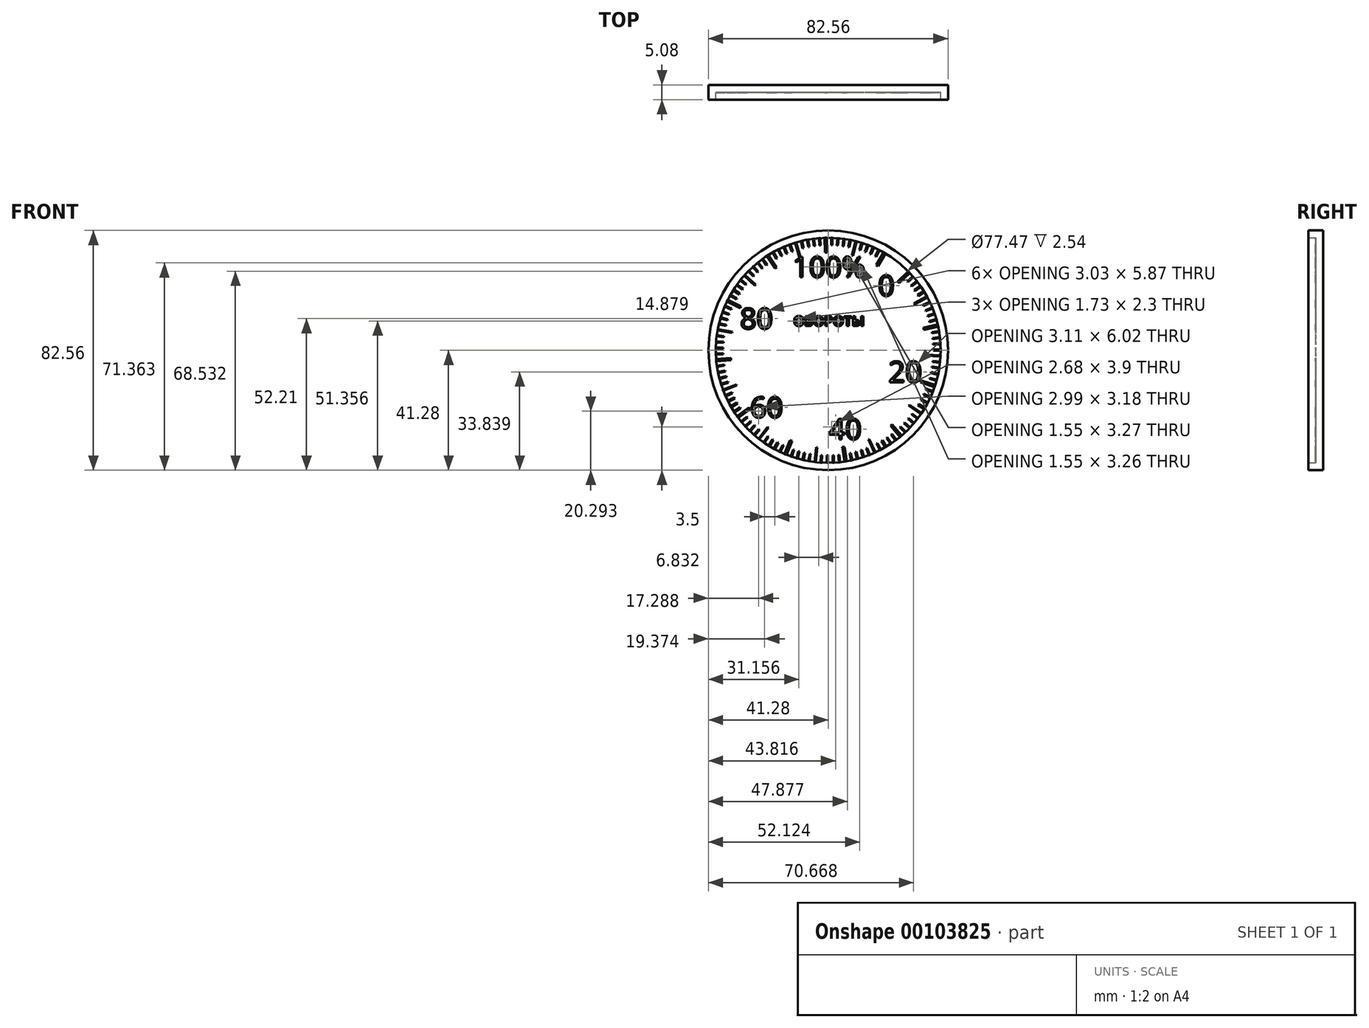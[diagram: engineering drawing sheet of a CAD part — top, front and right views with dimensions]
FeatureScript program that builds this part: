
annotation { "Feature Type Name" : "Feature", "Feature Type Description" : "" }
export const myFeature = defineFeature(function(context is Context, id is Id, definition is map)
    precondition{}
    {
        {
            var Q0;
            Q0=qCreatedBy(makeId("Front.planeOp"),FACE);
            var sketch = newSketch(context, id + "F0", { "sketchPlane" : qUnion([Q0])});
            skCircle(sketch, "E0", {"center": v(0, 0) * mm, "radius": 41.28 * mm});
            skSolve(sketch);
        }
        {
            var Q0;
            Q0=makeQuery(id+"F0.imprint","IMPRINT",FACE,{"disambiguationData":[TD([[makeQuery(id+"F0.imprint","IMPRINT",EDGE,{"derivedFrom":sQuery(id+"F0.wireOp",EDGE,"E0")}),1.0]])]});
            extrude(context, id + "F1", {"entities" : qUnion([Q0]), "depth" : 2.54 * mm});
        }
        {
            var Q0;
            Q0=makeQuery(id+"F1.opExtrude","CAP_FACE",FACE,{"disambiguationData":[OSD([sQuery(id+"F0.wireOp",EDGE,"E0")])],"isStart":false});
            var sketch = newSketch(context, id + "F2", { "sketchPlane" : qUnion([Q0])});
            skCircle(sketch, "E1.0", {"center": v(0, 0) * mm, "radius": 41.28 * mm});
            skCircle(sketch, "E2", {"center": v(0, 0) * mm, "radius": 38.74 * mm});
            skSolve(sketch);
        }
        {
            var Q0;
            Q0=makeQuery(id+"F2.imprint","IMPRINT",FACE,{"disambiguationData":[TD([[makeQuery(id+"F2.imprint","IMPRINT",EDGE,{"derivedFrom":sQuery(id+"F2.wireOp",EDGE,"E1.0")}),1.0]])]});
            extrude(context, id + "F3", {"entities" : qUnion([Q0]), "operationType" : NewBodyOperationType.ADD, "depth" : 2.54 * mm});
        }
        {
            var Q0;
            Q0=makeQuery(id+"F1.opExtrude","CAP_FACE",FACE,{"disambiguationData":[OSD([sQuery(id+"F0.wireOp",EDGE,"E0")])],"isStart":false});
            var sketch = newSketch(context, id + "F4", { "sketchPlane" : qUnion([Q0])});
            skLineSegment(sketch, "E3", {"start": v(0, 38.74) * mm, "end": v(0, -38.74) * mm, "construction": true});
            skLineSegment(sketch, "E4", {"start": v(0, 0) * mm, "end": v(27.86, 26.9) * mm, "construction": true});
            skLineSegment(sketch, "E5", {"start": v(27.6, 27.18) * mm, "end": v(23.94, 23.65) * mm, "construction": true});
            skLineSegment(sketch, "E6", {"start": v(23.94, 23.65) * mm, "end": v(24.47, 23.1) * mm, "construction": true});
            skLineSegment(sketch, "E7", {"start": v(24.47, 23.1) * mm, "end": v(28.13, 26.63) * mm, "construction": true});
            skLineSegment(sketch, "E8", {"start": v(28.13, 26.63) * mm, "end": v(27.6, 27.18) * mm, "construction": true});
            skLineSegment(sketch, "E9", {"start": v(27.73, 27.04) * mm, "end": v(24.08, 23.51) * mm, "construction": true});
            skLineSegment(sketch, "E10", {"start": v(24.08, 23.51) * mm, "end": v(24.34, 23.24) * mm, "construction": true});
            skLineSegment(sketch, "E11", {"start": v(24.34, 23.24) * mm, "end": v(28, 26.77) * mm, "construction": true});
            skLineSegment(sketch, "E12", {"start": v(28, 26.77) * mm, "end": v(27.73, 27.04) * mm});
            skPoint(sketch, "E13", {"position": v(24.2, 23.38) * mm});
            skLineSegment(sketch, "E14", {"start": v(27.73, 27.04) * mm, "end": v(25.9, 25.28) * mm});
            skLineSegment(sketch, "E15", {"start": v(25.9, 25.28) * mm, "end": v(26.17, 25) * mm});
            skLineSegment(sketch, "E16", {"start": v(26.17, 25) * mm, "end": v(28, 26.77) * mm});
            skLineSegment(sketch, "E17.1.0", {"start": v(27.5, 23.54) * mm, "end": v(29.41, 25.2) * mm});
            skLineSegment(sketch, "E17.1.1", {"start": v(29.41, 25.2) * mm, "end": v(29.17, 25.5) * mm});
            skLineSegment(sketch, "E17.1.2", {"start": v(29.17, 25.5) * mm, "end": v(27.24, 23.83) * mm});
            skLineSegment(sketch, "E17.1.3", {"start": v(27.24, 23.83) * mm, "end": v(27.5, 23.54) * mm});
            skLineSegment(sketch, "E17.2.0", {"start": v(28.74, 22) * mm, "end": v(30.75, 23.56) * mm});
            skLineSegment(sketch, "E17.2.1", {"start": v(30.75, 23.56) * mm, "end": v(30.51, 23.86) * mm});
            skLineSegment(sketch, "E17.2.2", {"start": v(30.51, 23.86) * mm, "end": v(28.5, 22.3) * mm});
            skLineSegment(sketch, "E17.2.3", {"start": v(28.5, 22.3) * mm, "end": v(28.74, 22) * mm});
            skLineSegment(sketch, "E17.3.0", {"start": v(29.9, 20.4) * mm, "end": v(31.99, 21.85) * mm});
            skLineSegment(sketch, "E17.3.1", {"start": v(31.99, 21.85) * mm, "end": v(31.77, 22.16) * mm});
            skLineSegment(sketch, "E17.3.2", {"start": v(31.77, 22.16) * mm, "end": v(29.68, 20.72) * mm});
            skLineSegment(sketch, "E17.3.3", {"start": v(29.68, 20.72) * mm, "end": v(29.9, 20.4) * mm});
            skLineSegment(sketch, "E17.4.0", {"start": v(30.96, 18.74) * mm, "end": v(33.13, 20.07) * mm});
            skLineSegment(sketch, "E17.4.1", {"start": v(33.13, 20.07) * mm, "end": v(32.93, 20.4) * mm});
            skLineSegment(sketch, "E17.4.2", {"start": v(32.93, 20.4) * mm, "end": v(30.76, 19.07) * mm});
            skLineSegment(sketch, "E17.4.3", {"start": v(30.76, 19.07) * mm, "end": v(30.96, 18.74) * mm});
            skLineSegment(sketch, "E17.5.0", {"start": v(31.94, 17.03) * mm, "end": v(34.17, 18.23) * mm});
            skLineSegment(sketch, "E17.5.1", {"start": v(34.17, 18.23) * mm, "end": v(34, 18.57) * mm});
            skLineSegment(sketch, "E17.5.2", {"start": v(34, 18.57) * mm, "end": v(31.76, 17.36) * mm});
            skLineSegment(sketch, "E17.5.3", {"start": v(31.76, 17.36) * mm, "end": v(31.94, 17.03) * mm});
            skLineSegment(sketch, "E17.6.0", {"start": v(32.82, 15.26) * mm, "end": v(35.12, 16.34) * mm});
            skLineSegment(sketch, "E17.6.1", {"start": v(35.12, 16.34) * mm, "end": v(34.96, 16.69) * mm});
            skLineSegment(sketch, "E17.6.2", {"start": v(34.96, 16.69) * mm, "end": v(32.66, 15.6) * mm});
            skLineSegment(sketch, "E17.6.3", {"start": v(32.66, 15.6) * mm, "end": v(32.82, 15.26) * mm});
            skLineSegment(sketch, "E17.7.0", {"start": v(33.6, 13.45) * mm, "end": v(35.96, 14.4) * mm});
            skLineSegment(sketch, "E17.7.1", {"start": v(35.96, 14.4) * mm, "end": v(35.81, 14.76) * mm});
            skLineSegment(sketch, "E17.7.2", {"start": v(35.81, 14.76) * mm, "end": v(33.46, 13.8) * mm});
            skLineSegment(sketch, "E17.7.3", {"start": v(33.46, 13.8) * mm, "end": v(33.6, 13.45) * mm});
            skLineSegment(sketch, "E17.8.0", {"start": v(34.29, 11.6) * mm, "end": v(36.7, 12.42) * mm});
            skLineSegment(sketch, "E17.8.1", {"start": v(36.7, 12.42) * mm, "end": v(36.57, 12.78) * mm});
            skLineSegment(sketch, "E17.8.2", {"start": v(36.57, 12.78) * mm, "end": v(34.16, 11.95) * mm});
            skLineSegment(sketch, "E17.8.3", {"start": v(34.16, 11.95) * mm, "end": v(34.29, 11.6) * mm});
            skLineSegment(sketch, "E17.9.0", {"start": v(34.87, 9.7) * mm, "end": v(37.31, 10.4) * mm});
            skLineSegment(sketch, "E17.9.1", {"start": v(37.31, 10.4) * mm, "end": v(37.2, 10.77) * mm});
            skLineSegment(sketch, "E17.9.2", {"start": v(37.2, 10.77) * mm, "end": v(34.76, 10.07) * mm});
            skLineSegment(sketch, "E17.9.3", {"start": v(34.76, 10.07) * mm, "end": v(34.87, 9.7) * mm});
            skLineSegment(sketch, "E17.10.0", {"start": v(35.35, 7.79) * mm, "end": v(37.82, 8.35) * mm});
            skLineSegment(sketch, "E17.10.1", {"start": v(37.82, 8.35) * mm, "end": v(37.74, 8.72) * mm});
            skLineSegment(sketch, "E17.10.2", {"start": v(37.74, 8.72) * mm, "end": v(35.26, 8.16) * mm});
            skLineSegment(sketch, "E17.10.3", {"start": v(35.26, 8.16) * mm, "end": v(35.35, 7.79) * mm});
            skLineSegment(sketch, "E17.11.0", {"start": v(35.72, 5.85) * mm, "end": v(38.22, 6.27) * mm});
            skLineSegment(sketch, "E17.11.1", {"start": v(38.22, 6.27) * mm, "end": v(38.16, 6.65) * mm});
            skLineSegment(sketch, "E17.11.2", {"start": v(38.16, 6.65) * mm, "end": v(35.66, 6.22) * mm});
            skLineSegment(sketch, "E17.11.3", {"start": v(35.66, 6.22) * mm, "end": v(35.72, 5.85) * mm});
            skLineSegment(sketch, "E17.12.0", {"start": v(35.98, 3.9) * mm, "end": v(38.5, 4.18) * mm});
            skLineSegment(sketch, "E17.12.1", {"start": v(38.5, 4.18) * mm, "end": v(38.47, 4.56) * mm});
            skLineSegment(sketch, "E17.12.2", {"start": v(38.47, 4.56) * mm, "end": v(35.94, 4.27) * mm});
            skLineSegment(sketch, "E17.12.3", {"start": v(35.94, 4.27) * mm, "end": v(35.98, 3.9) * mm});
            skLineSegment(sketch, "E17.13.0", {"start": v(36.14, 1.92) * mm, "end": v(38.68, 2.07) * mm});
            skLineSegment(sketch, "E17.13.1", {"start": v(38.68, 2.07) * mm, "end": v(38.66, 2.45) * mm});
            skLineSegment(sketch, "E17.13.2", {"start": v(38.66, 2.45) * mm, "end": v(36.12, 2.3) * mm});
            skLineSegment(sketch, "E17.13.3", {"start": v(36.12, 2.3) * mm, "end": v(36.14, 1.92) * mm});
            skLineSegment(sketch, "E17.14.0", {"start": v(36.2, -0.05) * mm, "end": v(38.73, -0.04) * mm});
            skLineSegment(sketch, "E17.14.1", {"start": v(38.73, -0.04) * mm, "end": v(38.73, 0.34) * mm});
            skLineSegment(sketch, "E17.14.2", {"start": v(38.73, 0.34) * mm, "end": v(36.2, 0.33) * mm});
            skLineSegment(sketch, "E17.14.3", {"start": v(36.2, 0.33) * mm, "end": v(36.2, -0.05) * mm});
            skLineSegment(sketch, "E17.15.0", {"start": v(36.14, -2.03) * mm, "end": v(38.67, -2.16) * mm});
            skLineSegment(sketch, "E17.15.1", {"start": v(38.67, -2.16) * mm, "end": v(38.7, -1.78) * mm});
            skLineSegment(sketch, "E17.15.2", {"start": v(38.7, -1.78) * mm, "end": v(36.16, -1.65) * mm});
            skLineSegment(sketch, "E17.15.3", {"start": v(36.16, -1.65) * mm, "end": v(36.14, -2.03) * mm});
            skLineSegment(sketch, "E17.16.0", {"start": v(35.97, -4) * mm, "end": v(38.5, -4.26) * mm});
            skLineSegment(sketch, "E17.16.1", {"start": v(38.5, -4.26) * mm, "end": v(38.54, -3.88) * mm});
            skLineSegment(sketch, "E17.16.2", {"start": v(38.54, -3.88) * mm, "end": v(36.01, -3.62) * mm});
            skLineSegment(sketch, "E17.16.3", {"start": v(36.01, -3.62) * mm, "end": v(35.97, -4) * mm});
            skLineSegment(sketch, "E17.17.0", {"start": v(35.7, -5.95) * mm, "end": v(38.2, -6.36) * mm});
            skLineSegment(sketch, "E17.17.1", {"start": v(38.2, -6.36) * mm, "end": v(38.27, -5.98) * mm});
            skLineSegment(sketch, "E17.17.2", {"start": v(38.27, -5.98) * mm, "end": v(35.76, -5.58) * mm});
            skLineSegment(sketch, "E17.17.3", {"start": v(35.76, -5.58) * mm, "end": v(35.7, -5.95) * mm});
            skLineSegment(sketch, "E17.18.0", {"start": v(35.32, -7.9) * mm, "end": v(37.8, -8.43) * mm});
            skLineSegment(sketch, "E17.18.1", {"start": v(37.8, -8.43) * mm, "end": v(37.89, -8.06) * mm});
            skLineSegment(sketch, "E17.18.2", {"start": v(37.89, -8.06) * mm, "end": v(35.4, -7.52) * mm});
            skLineSegment(sketch, "E17.18.3", {"start": v(35.4, -7.52) * mm, "end": v(35.32, -7.9) * mm});
            skLineSegment(sketch, "E17.19.0", {"start": v(34.84, -9.8) * mm, "end": v(37.29, -10.48) * mm});
            skLineSegment(sketch, "E17.19.1", {"start": v(37.29, -10.48) * mm, "end": v(37.4, -10.11) * mm});
            skLineSegment(sketch, "E17.19.2", {"start": v(37.4, -10.11) * mm, "end": v(34.94, -9.44) * mm});
            skLineSegment(sketch, "E17.19.3", {"start": v(34.94, -9.44) * mm, "end": v(34.84, -9.8) * mm});
            skLineSegment(sketch, "E17.20.0", {"start": v(34.25, -11.7) * mm, "end": v(36.66, -12.5) * mm});
            skLineSegment(sketch, "E17.20.1", {"start": v(36.66, -12.5) * mm, "end": v(36.78, -12.14) * mm});
            skLineSegment(sketch, "E17.20.2", {"start": v(36.78, -12.14) * mm, "end": v(34.37, -11.33) * mm});
            skLineSegment(sketch, "E17.20.3", {"start": v(34.37, -11.33) * mm, "end": v(34.25, -11.7) * mm});
            skLineSegment(sketch, "E17.21.0", {"start": v(33.56, -13.54) * mm, "end": v(35.93, -14.48) * mm});
            skLineSegment(sketch, "E17.21.1", {"start": v(35.93, -14.48) * mm, "end": v(36.07, -14.13) * mm});
            skLineSegment(sketch, "E17.21.2", {"start": v(36.07, -14.13) * mm, "end": v(33.7, -13.19) * mm});
            skLineSegment(sketch, "E17.21.3", {"start": v(33.7, -13.19) * mm, "end": v(33.56, -13.54) * mm});
            skLineSegment(sketch, "E17.22.0", {"start": v(32.78, -15.35) * mm, "end": v(35.08, -16.42) * mm});
            skLineSegment(sketch, "E17.22.1", {"start": v(35.08, -16.42) * mm, "end": v(35.24, -16.07) * mm});
            skLineSegment(sketch, "E17.22.2", {"start": v(35.24, -16.07) * mm, "end": v(32.94, -15) * mm});
            skLineSegment(sketch, "E17.22.3", {"start": v(32.94, -15) * mm, "end": v(32.78, -15.35) * mm});
            skLineSegment(sketch, "E17.23.0", {"start": v(31.89, -17.12) * mm, "end": v(34.13, -18.3) * mm});
            skLineSegment(sketch, "E17.23.1", {"start": v(34.13, -18.3) * mm, "end": v(34.31, -17.97) * mm});
            skLineSegment(sketch, "E17.23.2", {"start": v(34.31, -17.97) * mm, "end": v(32.07, -16.78) * mm});
            skLineSegment(sketch, "E17.23.3", {"start": v(32.07, -16.78) * mm, "end": v(31.89, -17.12) * mm});
            skLineSegment(sketch, "E17.24.0", {"start": v(30.9, -18.83) * mm, "end": v(33.08, -20.14) * mm});
            skLineSegment(sketch, "E17.24.1", {"start": v(33.08, -20.14) * mm, "end": v(33.28, -19.82) * mm});
            skLineSegment(sketch, "E17.24.2", {"start": v(33.28, -19.82) * mm, "end": v(31.1, -18.5) * mm});
            skLineSegment(sketch, "E17.24.3", {"start": v(31.1, -18.5) * mm, "end": v(30.9, -18.83) * mm});
            skLineSegment(sketch, "E17.25.0", {"start": v(29.83, -20.5) * mm, "end": v(31.94, -21.92) * mm});
            skLineSegment(sketch, "E17.25.1", {"start": v(31.94, -21.92) * mm, "end": v(32.15, -21.6) * mm});
            skLineSegment(sketch, "E17.25.2", {"start": v(32.15, -21.6) * mm, "end": v(30.05, -20.18) * mm});
            skLineSegment(sketch, "E17.25.3", {"start": v(30.05, -20.18) * mm, "end": v(29.83, -20.5) * mm});
            skLineSegment(sketch, "E17.26.0", {"start": v(28.67, -22.09) * mm, "end": v(30.7, -23.63) * mm});
            skLineSegment(sketch, "E17.26.1", {"start": v(30.7, -23.63) * mm, "end": v(30.92, -23.33) * mm});
            skLineSegment(sketch, "E17.26.2", {"start": v(30.92, -23.33) * mm, "end": v(28.9, -21.79) * mm});
            skLineSegment(sketch, "E17.26.3", {"start": v(28.9, -21.79) * mm, "end": v(28.67, -22.09) * mm});
            skLineSegment(sketch, "E17.27.0", {"start": v(27.42, -23.62) * mm, "end": v(29.36, -25.27) * mm});
            skLineSegment(sketch, "E17.27.1", {"start": v(29.36, -25.27) * mm, "end": v(29.6, -24.98) * mm});
            skLineSegment(sketch, "E17.27.2", {"start": v(29.6, -24.98) * mm, "end": v(27.67, -23.33) * mm});
            skLineSegment(sketch, "E17.27.3", {"start": v(27.67, -23.33) * mm, "end": v(27.42, -23.62) * mm});
            skLineSegment(sketch, "E17.28.0", {"start": v(26.1, -25.08) * mm, "end": v(27.94, -26.83) * mm});
            skLineSegment(sketch, "E17.28.1", {"start": v(27.94, -26.83) * mm, "end": v(28.2, -26.56) * mm});
            skLineSegment(sketch, "E17.28.2", {"start": v(28.2, -26.56) * mm, "end": v(26.36, -24.8) * mm});
            skLineSegment(sketch, "E17.28.3", {"start": v(26.36, -24.8) * mm, "end": v(26.1, -25.08) * mm});
            skLineSegment(sketch, "E17.29.0", {"start": v(24.69, -26.47) * mm, "end": v(26.43, -28.32) * mm});
            skLineSegment(sketch, "E17.29.1", {"start": v(26.43, -28.32) * mm, "end": v(26.7, -28.06) * mm});
            skLineSegment(sketch, "E17.29.2", {"start": v(26.7, -28.06) * mm, "end": v(24.97, -26.2) * mm});
            skLineSegment(sketch, "E17.29.3", {"start": v(24.97, -26.2) * mm, "end": v(24.69, -26.47) * mm});
            skLineSegment(sketch, "E17.30.0", {"start": v(23.2, -27.78) * mm, "end": v(24.85, -29.72) * mm});
            skLineSegment(sketch, "E17.30.1", {"start": v(24.85, -29.72) * mm, "end": v(25.14, -29.47) * mm});
            skLineSegment(sketch, "E17.30.2", {"start": v(25.14, -29.47) * mm, "end": v(23.5, -27.53) * mm});
            skLineSegment(sketch, "E17.30.3", {"start": v(23.5, -27.53) * mm, "end": v(23.2, -27.78) * mm});
            skLineSegment(sketch, "E17.31.0", {"start": v(21.66, -29) * mm, "end": v(23.19, -31.03) * mm});
            skLineSegment(sketch, "E17.31.1", {"start": v(23.19, -31.03) * mm, "end": v(23.5, -30.8) * mm});
            skLineSegment(sketch, "E17.31.2", {"start": v(23.5, -30.8) * mm, "end": v(21.96, -28.77) * mm});
            skLineSegment(sketch, "E17.31.3", {"start": v(21.96, -28.77) * mm, "end": v(21.66, -29) * mm});
            skLineSegment(sketch, "E17.32.0", {"start": v(20.04, -30.14) * mm, "end": v(21.46, -32.25) * mm});
            skLineSegment(sketch, "E17.32.1", {"start": v(21.46, -32.25) * mm, "end": v(21.78, -32.03) * mm});
            skLineSegment(sketch, "E17.32.2", {"start": v(21.78, -32.03) * mm, "end": v(20.36, -29.93) * mm});
            skLineSegment(sketch, "E17.32.3", {"start": v(20.36, -29.93) * mm, "end": v(20.04, -30.14) * mm});
            skLineSegment(sketch, "E17.33.0", {"start": v(18.37, -31.19) * mm, "end": v(19.67, -33.37) * mm});
            skLineSegment(sketch, "E17.33.1", {"start": v(19.67, -33.37) * mm, "end": v(20, -33.17) * mm});
            skLineSegment(sketch, "E17.33.2", {"start": v(20, -33.17) * mm, "end": v(18.7, -31) * mm});
            skLineSegment(sketch, "E17.33.3", {"start": v(18.7, -31) * mm, "end": v(18.37, -31.19) * mm});
            skLineSegment(sketch, "E17.34.0", {"start": v(16.64, -32.14) * mm, "end": v(17.82, -34.4) * mm});
            skLineSegment(sketch, "E17.34.1", {"start": v(17.82, -34.4) * mm, "end": v(18.16, -34.22) * mm});
            skLineSegment(sketch, "E17.34.2", {"start": v(18.16, -34.22) * mm, "end": v(16.98, -31.97) * mm});
            skLineSegment(sketch, "E17.34.3", {"start": v(16.98, -31.97) * mm, "end": v(16.64, -32.14) * mm});
            skLineSegment(sketch, "E17.35.0", {"start": v(14.86, -33) * mm, "end": v(15.92, -35.31) * mm});
            skLineSegment(sketch, "E17.35.1", {"start": v(15.92, -35.31) * mm, "end": v(16.26, -35.16) * mm});
            skLineSegment(sketch, "E17.35.2", {"start": v(16.26, -35.16) * mm, "end": v(15.2, -32.84) * mm});
            skLineSegment(sketch, "E17.35.3", {"start": v(15.2, -32.84) * mm, "end": v(14.86, -33) * mm});
            skLineSegment(sketch, "E17.36.0", {"start": v(13.04, -33.76) * mm, "end": v(13.97, -36.13) * mm});
            skLineSegment(sketch, "E17.36.1", {"start": v(13.97, -36.13) * mm, "end": v(14.32, -35.99) * mm});
            skLineSegment(sketch, "E17.36.2", {"start": v(14.32, -35.99) * mm, "end": v(13.4, -33.62) * mm});
            skLineSegment(sketch, "E17.36.3", {"start": v(13.4, -33.62) * mm, "end": v(13.04, -33.76) * mm});
            skLineSegment(sketch, "E17.37.0", {"start": v(11.18, -34.42) * mm, "end": v(11.98, -36.84) * mm});
            skLineSegment(sketch, "E17.37.1", {"start": v(11.98, -36.84) * mm, "end": v(12.34, -36.72) * mm});
            skLineSegment(sketch, "E17.37.2", {"start": v(12.34, -36.72) * mm, "end": v(11.54, -34.3) * mm});
            skLineSegment(sketch, "E17.37.3", {"start": v(11.54, -34.3) * mm, "end": v(11.18, -34.42) * mm});
            skLineSegment(sketch, "E17.38.0", {"start": v(9.28, -34.98) * mm, "end": v(9.95, -37.44) * mm});
            skLineSegment(sketch, "E17.38.1", {"start": v(9.95, -37.44) * mm, "end": v(10.32, -37.34) * mm});
            skLineSegment(sketch, "E17.38.2", {"start": v(10.32, -37.34) * mm, "end": v(9.65, -34.88) * mm});
            skLineSegment(sketch, "E17.38.3", {"start": v(9.65, -34.88) * mm, "end": v(9.28, -34.98) * mm});
            skLineSegment(sketch, "E17.39.0", {"start": v(7.36, -35.44) * mm, "end": v(7.9, -37.92) * mm});
            skLineSegment(sketch, "E17.39.1", {"start": v(7.9, -37.92) * mm, "end": v(8.26, -37.84) * mm});
            skLineSegment(sketch, "E17.39.2", {"start": v(8.26, -37.84) * mm, "end": v(7.73, -35.36) * mm});
            skLineSegment(sketch, "E17.39.3", {"start": v(7.73, -35.36) * mm, "end": v(7.36, -35.44) * mm});
            skLineSegment(sketch, "E17.40.0", {"start": v(5.42, -35.79) * mm, "end": v(5.81, -38.3) * mm});
            skLineSegment(sketch, "E17.40.1", {"start": v(5.81, -38.3) * mm, "end": v(6.19, -38.24) * mm});
            skLineSegment(sketch, "E17.40.2", {"start": v(6.19, -38.24) * mm, "end": v(5.8, -35.73) * mm});
            skLineSegment(sketch, "E17.40.3", {"start": v(5.8, -35.73) * mm, "end": v(5.42, -35.79) * mm});
            skLineSegment(sketch, "E17.41.0", {"start": v(3.46, -36.03) * mm, "end": v(3.71, -38.56) * mm});
            skLineSegment(sketch, "E17.41.1", {"start": v(3.71, -38.56) * mm, "end": v(4.1, -38.52) * mm});
            skLineSegment(sketch, "E17.41.2", {"start": v(4.1, -38.52) * mm, "end": v(3.84, -36) * mm});
            skLineSegment(sketch, "E17.41.3", {"start": v(3.84, -36) * mm, "end": v(3.46, -36.03) * mm});
            skLineSegment(sketch, "E17.42.0", {"start": v(1.49, -36.16) * mm, "end": v(1.6, -38.7) * mm});
            skLineSegment(sketch, "E17.42.1", {"start": v(1.6, -38.7) * mm, "end": v(1.98, -38.68) * mm});
            skLineSegment(sketch, "E17.42.2", {"start": v(1.98, -38.68) * mm, "end": v(1.87, -36.15) * mm});
            skLineSegment(sketch, "E17.42.3", {"start": v(1.87, -36.15) * mm, "end": v(1.49, -36.16) * mm});
            skLineSegment(sketch, "E17.43.0", {"start": v(-0.49, -36.2) * mm, "end": v(-0.51, -38.73) * mm});
            skLineSegment(sketch, "E17.43.1", {"start": v(-0.51, -38.73) * mm, "end": v(-0.13, -38.73) * mm});
            skLineSegment(sketch, "E17.43.2", {"start": v(-0.13, -38.73) * mm, "end": v(-0.1, -36.2) * mm});
            skLineSegment(sketch, "E17.43.3", {"start": v(-0.1, -36.2) * mm, "end": v(-0.49, -36.2) * mm});
            skLineSegment(sketch, "E17.44.0", {"start": v(-2.46, -36.11) * mm, "end": v(-2.62, -38.65) * mm});
            skLineSegment(sketch, "E17.44.1", {"start": v(-2.62, -38.65) * mm, "end": v(-2.24, -38.67) * mm});
            skLineSegment(sketch, "E17.44.2", {"start": v(-2.24, -38.67) * mm, "end": v(-2.08, -36.13) * mm});
            skLineSegment(sketch, "E17.44.3", {"start": v(-2.08, -36.13) * mm, "end": v(-2.46, -36.11) * mm});
            skLineSegment(sketch, "E17.45.0", {"start": v(-4.43, -35.92) * mm, "end": v(-4.73, -38.45) * mm});
            skLineSegment(sketch, "E17.45.1", {"start": v(-4.73, -38.45) * mm, "end": v(-4.35, -38.5) * mm});
            skLineSegment(sketch, "E17.45.2", {"start": v(-4.35, -38.5) * mm, "end": v(-4.05, -35.97) * mm});
            skLineSegment(sketch, "E17.45.3", {"start": v(-4.05, -35.97) * mm, "end": v(-4.43, -35.92) * mm});
            skLineSegment(sketch, "E17.46.0", {"start": v(-6.38, -35.63) * mm, "end": v(-6.82, -38.13) * mm});
            skLineSegment(sketch, "E17.46.1", {"start": v(-6.82, -38.13) * mm, "end": v(-6.44, -38.2) * mm});
            skLineSegment(sketch, "E17.46.2", {"start": v(-6.44, -38.2) * mm, "end": v(-6, -35.7) * mm});
            skLineSegment(sketch, "E17.46.3", {"start": v(-6, -35.7) * mm, "end": v(-6.38, -35.63) * mm});
            skLineSegment(sketch, "E17.47.0", {"start": v(-8.32, -35.23) * mm, "end": v(-8.89, -37.7) * mm});
            skLineSegment(sketch, "E17.47.1", {"start": v(-8.89, -37.7) * mm, "end": v(-8.52, -37.79) * mm});
            skLineSegment(sketch, "E17.47.2", {"start": v(-8.52, -37.79) * mm, "end": v(-7.95, -35.31) * mm});
            skLineSegment(sketch, "E17.47.3", {"start": v(-7.95, -35.31) * mm, "end": v(-8.32, -35.23) * mm});
            skLineSegment(sketch, "E17.48.0", {"start": v(-10.23, -34.72) * mm, "end": v(-10.93, -37.16) * mm});
            skLineSegment(sketch, "E17.48.1", {"start": v(-10.93, -37.16) * mm, "end": v(-10.56, -37.27) * mm});
            skLineSegment(sketch, "E17.48.2", {"start": v(-10.56, -37.27) * mm, "end": v(-9.86, -34.83) * mm});
            skLineSegment(sketch, "E17.48.3", {"start": v(-9.86, -34.83) * mm, "end": v(-10.23, -34.72) * mm});
            skLineSegment(sketch, "E17.49.0", {"start": v(-12.1, -34.11) * mm, "end": v(-12.94, -36.5) * mm});
            skLineSegment(sketch, "E17.49.1", {"start": v(-12.94, -36.5) * mm, "end": v(-12.58, -36.63) * mm});
            skLineSegment(sketch, "E17.49.2", {"start": v(-12.58, -36.63) * mm, "end": v(-11.74, -34.24) * mm});
            skLineSegment(sketch, "E17.49.3", {"start": v(-11.74, -34.24) * mm, "end": v(-12.1, -34.11) * mm});
            skLineSegment(sketch, "E17.50.0", {"start": v(-13.95, -33.4) * mm, "end": v(-14.91, -35.75) * mm});
            skLineSegment(sketch, "E17.50.1", {"start": v(-14.91, -35.75) * mm, "end": v(-14.56, -35.9) * mm});
            skLineSegment(sketch, "E17.50.2", {"start": v(-14.56, -35.9) * mm, "end": v(-13.6, -33.54) * mm});
            skLineSegment(sketch, "E17.50.3", {"start": v(-13.6, -33.54) * mm, "end": v(-13.95, -33.4) * mm});
            skLineSegment(sketch, "E17.51.0", {"start": v(-15.75, -32.59) * mm, "end": v(-16.84, -34.88) * mm});
            skLineSegment(sketch, "E17.51.1", {"start": v(-16.84, -34.88) * mm, "end": v(-16.5, -35.05) * mm});
            skLineSegment(sketch, "E17.51.2", {"start": v(-16.5, -35.05) * mm, "end": v(-15.4, -32.75) * mm});
            skLineSegment(sketch, "E17.51.3", {"start": v(-15.4, -32.75) * mm, "end": v(-15.75, -32.59) * mm});
            skLineSegment(sketch, "E17.52.0", {"start": v(-17.5, -31.68) * mm, "end": v(-18.72, -33.91) * mm});
            skLineSegment(sketch, "E17.52.1", {"start": v(-18.72, -33.91) * mm, "end": v(-18.39, -34.1) * mm});
            skLineSegment(sketch, "E17.52.2", {"start": v(-18.39, -34.1) * mm, "end": v(-17.17, -31.86) * mm});
            skLineSegment(sketch, "E17.52.3", {"start": v(-17.17, -31.86) * mm, "end": v(-17.5, -31.68) * mm});
            skLineSegment(sketch, "E17.53.0", {"start": v(-19.2, -30.68) * mm, "end": v(-20.54, -32.84) * mm});
            skLineSegment(sketch, "E17.53.1", {"start": v(-20.54, -32.84) * mm, "end": v(-20.22, -33.04) * mm});
            skLineSegment(sketch, "E17.53.2", {"start": v(-20.22, -33.04) * mm, "end": v(-18.88, -30.88) * mm});
            skLineSegment(sketch, "E17.53.3", {"start": v(-18.88, -30.88) * mm, "end": v(-19.2, -30.68) * mm});
            skLineSegment(sketch, "E17.54.0", {"start": v(-20.85, -29.59) * mm, "end": v(-22.3, -31.67) * mm});
            skLineSegment(sketch, "E17.54.1", {"start": v(-22.3, -31.67) * mm, "end": v(-22, -31.89) * mm});
            skLineSegment(sketch, "E17.54.2", {"start": v(-22, -31.89) * mm, "end": v(-20.54, -29.8) * mm});
            skLineSegment(sketch, "E17.54.3", {"start": v(-20.54, -29.8) * mm, "end": v(-20.85, -29.59) * mm});
            skLineSegment(sketch, "E17.55.0", {"start": v(-22.43, -28.4) * mm, "end": v(-24, -30.4) * mm});
            skLineSegment(sketch, "E17.55.1", {"start": v(-24, -30.4) * mm, "end": v(-23.7, -30.64) * mm});
            skLineSegment(sketch, "E17.55.2", {"start": v(-23.7, -30.64) * mm, "end": v(-22.13, -28.64) * mm});
            skLineSegment(sketch, "E17.55.3", {"start": v(-22.13, -28.64) * mm, "end": v(-22.43, -28.4) * mm});
            skLineSegment(sketch, "E17.56.0", {"start": v(-23.95, -27.14) * mm, "end": v(-25.62, -29.05) * mm});
            skLineSegment(sketch, "E17.56.1", {"start": v(-25.62, -29.05) * mm, "end": v(-25.33, -29.3) * mm});
            skLineSegment(sketch, "E17.56.2", {"start": v(-25.33, -29.3) * mm, "end": v(-23.66, -27.39) * mm});
            skLineSegment(sketch, "E17.56.3", {"start": v(-23.66, -27.39) * mm, "end": v(-23.95, -27.14) * mm});
            skLineSegment(sketch, "E17.57.0", {"start": v(-25.4, -25.8) * mm, "end": v(-27.17, -27.61) * mm});
            skLineSegment(sketch, "E17.57.1", {"start": v(-27.17, -27.61) * mm, "end": v(-26.9, -27.88) * mm});
            skLineSegment(sketch, "E17.57.2", {"start": v(-26.9, -27.88) * mm, "end": v(-25.12, -26.06) * mm});
            skLineSegment(sketch, "E17.57.3", {"start": v(-25.12, -26.06) * mm, "end": v(-25.4, -25.8) * mm});
            skLineSegment(sketch, "E17.58.0", {"start": v(-26.76, -24.37) * mm, "end": v(-28.63, -26.09) * mm});
            skLineSegment(sketch, "E17.58.1", {"start": v(-28.63, -26.09) * mm, "end": v(-28.38, -26.37) * mm});
            skLineSegment(sketch, "E17.58.2", {"start": v(-28.38, -26.37) * mm, "end": v(-26.5, -24.65) * mm});
            skLineSegment(sketch, "E17.58.3", {"start": v(-26.5, -24.65) * mm, "end": v(-26.76, -24.37) * mm});
            skLineSegment(sketch, "E17.59.0", {"start": v(-28.05, -22.87) * mm, "end": v(-30.01, -24.49) * mm});
            skLineSegment(sketch, "E17.59.1", {"start": v(-30.01, -24.49) * mm, "end": v(-29.77, -24.78) * mm});
            skLineSegment(sketch, "E17.59.2", {"start": v(-29.77, -24.78) * mm, "end": v(-27.81, -23.16) * mm});
            skLineSegment(sketch, "E17.59.3", {"start": v(-27.81, -23.16) * mm, "end": v(-28.05, -22.87) * mm});
            skLineSegment(sketch, "E17.60.0", {"start": v(-29.26, -21.3) * mm, "end": v(-31.3, -22.81) * mm});
            skLineSegment(sketch, "E17.60.1", {"start": v(-31.3, -22.81) * mm, "end": v(-31.08, -23.12) * mm});
            skLineSegment(sketch, "E17.60.2", {"start": v(-31.08, -23.12) * mm, "end": v(-29.03, -21.61) * mm});
            skLineSegment(sketch, "E17.60.3", {"start": v(-29.03, -21.61) * mm, "end": v(-29.26, -21.3) * mm});
            skLineSegment(sketch, "E17.61.0", {"start": v(-30.38, -19.68) * mm, "end": v(-32.5, -21.07) * mm});
            skLineSegment(sketch, "E17.61.1", {"start": v(-32.5, -21.07) * mm, "end": v(-32.3, -21.39) * mm});
            skLineSegment(sketch, "E17.61.2", {"start": v(-32.3, -21.39) * mm, "end": v(-30.17, -20) * mm});
            skLineSegment(sketch, "E17.61.3", {"start": v(-30.17, -20) * mm, "end": v(-30.38, -19.68) * mm});
            skLineSegment(sketch, "E17.62.0", {"start": v(-31.4, -18) * mm, "end": v(-33.6, -19.27) * mm});
            skLineSegment(sketch, "E17.62.1", {"start": v(-33.6, -19.27) * mm, "end": v(-33.41, -19.6) * mm});
            skLineSegment(sketch, "E17.62.2", {"start": v(-33.41, -19.6) * mm, "end": v(-31.21, -18.32) * mm});
            skLineSegment(sketch, "E17.62.3", {"start": v(-31.21, -18.32) * mm, "end": v(-31.4, -18) * mm});
            skLineSegment(sketch, "E17.63.0", {"start": v(-32.34, -16.25) * mm, "end": v(-34.6, -17.4) * mm});
            skLineSegment(sketch, "E17.63.1", {"start": v(-34.6, -17.4) * mm, "end": v(-34.43, -17.74) * mm});
            skLineSegment(sketch, "E17.63.2", {"start": v(-34.43, -17.74) * mm, "end": v(-32.17, -16.6) * mm});
            skLineSegment(sketch, "E17.63.3", {"start": v(-32.17, -16.6) * mm, "end": v(-32.34, -16.25) * mm});
            skLineSegment(sketch, "E17.64.0", {"start": v(-33.18, -14.46) * mm, "end": v(-35.5, -15.5) * mm});
            skLineSegment(sketch, "E17.64.1", {"start": v(-35.5, -15.5) * mm, "end": v(-35.35, -15.84) * mm});
            skLineSegment(sketch, "E17.64.2", {"start": v(-35.35, -15.84) * mm, "end": v(-33.02, -14.81) * mm});
            skLineSegment(sketch, "E17.64.3", {"start": v(-33.02, -14.81) * mm, "end": v(-33.18, -14.46) * mm});
            skLineSegment(sketch, "E17.65.0", {"start": v(-33.92, -12.63) * mm, "end": v(-36.3, -13.53) * mm});
            skLineSegment(sketch, "E17.65.1", {"start": v(-36.3, -13.53) * mm, "end": v(-36.16, -13.89) * mm});
            skLineSegment(sketch, "E17.65.2", {"start": v(-36.16, -13.89) * mm, "end": v(-33.78, -12.99) * mm});
            skLineSegment(sketch, "E17.65.3", {"start": v(-33.78, -12.99) * mm, "end": v(-33.92, -12.63) * mm});
            skLineSegment(sketch, "E17.66.0", {"start": v(-34.56, -10.76) * mm, "end": v(-36.98, -11.53) * mm});
            skLineSegment(sketch, "E17.66.1", {"start": v(-36.98, -11.53) * mm, "end": v(-36.86, -11.9) * mm});
            skLineSegment(sketch, "E17.66.2", {"start": v(-36.86, -11.9) * mm, "end": v(-34.44, -11.13) * mm});
            skLineSegment(sketch, "E17.66.3", {"start": v(-34.44, -11.13) * mm, "end": v(-34.56, -10.76) * mm});
            skLineSegment(sketch, "E17.67.0", {"start": v(-35.1, -8.86) * mm, "end": v(-37.55, -9.5) * mm});
            skLineSegment(sketch, "E17.67.1", {"start": v(-37.55, -9.5) * mm, "end": v(-37.46, -9.86) * mm});
            skLineSegment(sketch, "E17.67.2", {"start": v(-37.46, -9.86) * mm, "end": v(-35, -9.23) * mm});
            skLineSegment(sketch, "E17.67.3", {"start": v(-35, -9.23) * mm, "end": v(-35.1, -8.86) * mm});
            skLineSegment(sketch, "E17.68.0", {"start": v(-35.52, -6.93) * mm, "end": v(-38.02, -7.43) * mm});
            skLineSegment(sketch, "E17.68.1", {"start": v(-38.02, -7.43) * mm, "end": v(-37.94, -7.8) * mm});
            skLineSegment(sketch, "E17.68.2", {"start": v(-37.94, -7.8) * mm, "end": v(-35.45, -7.3) * mm});
            skLineSegment(sketch, "E17.68.3", {"start": v(-35.45, -7.3) * mm, "end": v(-35.52, -6.93) * mm});
            skLineSegment(sketch, "E17.69.0", {"start": v(-35.85, -4.99) * mm, "end": v(-38.36, -5.35) * mm});
            skLineSegment(sketch, "E17.69.1", {"start": v(-38.36, -5.35) * mm, "end": v(-38.3, -5.73) * mm});
            skLineSegment(sketch, "E17.69.2", {"start": v(-38.3, -5.73) * mm, "end": v(-35.8, -5.36) * mm});
            skLineSegment(sketch, "E17.69.3", {"start": v(-35.8, -5.36) * mm, "end": v(-35.85, -4.99) * mm});
            skLineSegment(sketch, "E17.70.0", {"start": v(-36.07, -3.02) * mm, "end": v(-38.6, -3.25) * mm});
            skLineSegment(sketch, "E17.70.1", {"start": v(-38.6, -3.25) * mm, "end": v(-38.56, -3.63) * mm});
            skLineSegment(sketch, "E17.70.2", {"start": v(-38.56, -3.63) * mm, "end": v(-36.03, -3.4) * mm});
            skLineSegment(sketch, "E17.70.3", {"start": v(-36.03, -3.4) * mm, "end": v(-36.07, -3.02) * mm});
            skLineSegment(sketch, "E17.71.0", {"start": v(-36.18, -1.05) * mm, "end": v(-38.72, -1.14) * mm});
            skLineSegment(sketch, "E17.71.1", {"start": v(-38.72, -1.14) * mm, "end": v(-38.7, -1.52) * mm});
            skLineSegment(sketch, "E17.71.2", {"start": v(-38.7, -1.52) * mm, "end": v(-36.17, -1.43) * mm});
            skLineSegment(sketch, "E17.71.3", {"start": v(-36.17, -1.43) * mm, "end": v(-36.18, -1.05) * mm});
            skLineSegment(sketch, "E17.72.0", {"start": v(-36.18, 0.93) * mm, "end": v(-38.72, 0.98) * mm});
            skLineSegment(sketch, "E17.72.1", {"start": v(-38.72, 0.98) * mm, "end": v(-38.73, 0.6) * mm});
            skLineSegment(sketch, "E17.72.2", {"start": v(-38.73, 0.6) * mm, "end": v(-36.2, 0.54) * mm});
            skLineSegment(sketch, "E17.72.3", {"start": v(-36.2, 0.54) * mm, "end": v(-36.18, 0.93) * mm});
            skLineSegment(sketch, "E17.73.0", {"start": v(-36.08, 2.9) * mm, "end": v(-38.61, 3.09) * mm});
            skLineSegment(sketch, "E17.73.1", {"start": v(-38.61, 3.09) * mm, "end": v(-38.64, 2.7) * mm});
            skLineSegment(sketch, "E17.73.2", {"start": v(-38.64, 2.7) * mm, "end": v(-36.1, 2.52) * mm});
            skLineSegment(sketch, "E17.73.3", {"start": v(-36.1, 2.52) * mm, "end": v(-36.08, 2.9) * mm});
            skLineSegment(sketch, "E17.74.0", {"start": v(-35.87, 4.86) * mm, "end": v(-38.39, 5.19) * mm});
            skLineSegment(sketch, "E17.74.1", {"start": v(-38.39, 5.19) * mm, "end": v(-38.43, 4.81) * mm});
            skLineSegment(sketch, "E17.74.2", {"start": v(-38.43, 4.81) * mm, "end": v(-35.92, 4.48) * mm});
            skLineSegment(sketch, "E17.74.3", {"start": v(-35.92, 4.48) * mm, "end": v(-35.87, 4.86) * mm});
            skLineSegment(sketch, "E17.75.0", {"start": v(-35.55, 6.81) * mm, "end": v(-38.05, 7.28) * mm});
            skLineSegment(sketch, "E17.75.1", {"start": v(-38.05, 7.28) * mm, "end": v(-38.12, 6.9) * mm});
            skLineSegment(sketch, "E17.75.2", {"start": v(-38.12, 6.9) * mm, "end": v(-35.62, 6.44) * mm});
            skLineSegment(sketch, "E17.75.3", {"start": v(-35.62, 6.44) * mm, "end": v(-35.55, 6.81) * mm});
            skLineSegment(sketch, "E17.76.0", {"start": v(-35.12, 8.74) * mm, "end": v(-37.6, 9.34) * mm});
            skLineSegment(sketch, "E17.76.1", {"start": v(-37.6, 9.34) * mm, "end": v(-37.68, 8.97) * mm});
            skLineSegment(sketch, "E17.76.2", {"start": v(-37.68, 8.97) * mm, "end": v(-35.21, 8.37) * mm});
            skLineSegment(sketch, "E17.76.3", {"start": v(-35.21, 8.37) * mm, "end": v(-35.12, 8.74) * mm});
            skLineSegment(sketch, "E17.77.0", {"start": v(-34.6, 10.64) * mm, "end": v(-37.03, 11.38) * mm});
            skLineSegment(sketch, "E17.77.1", {"start": v(-37.03, 11.38) * mm, "end": v(-37.14, 11.01) * mm});
            skLineSegment(sketch, "E17.77.2", {"start": v(-37.14, 11.01) * mm, "end": v(-34.7, 10.28) * mm});
            skLineSegment(sketch, "E17.77.3", {"start": v(-34.7, 10.28) * mm, "end": v(-34.6, 10.64) * mm});
            skLineSegment(sketch, "E17.78.0", {"start": v(-33.96, 12.51) * mm, "end": v(-36.35, 13.38) * mm});
            skLineSegment(sketch, "E17.78.1", {"start": v(-36.35, 13.38) * mm, "end": v(-36.48, 13.02) * mm});
            skLineSegment(sketch, "E17.78.2", {"start": v(-36.48, 13.02) * mm, "end": v(-34.1, 12.16) * mm});
            skLineSegment(sketch, "E17.78.3", {"start": v(-34.1, 12.16) * mm, "end": v(-33.96, 12.51) * mm});
            skLineSegment(sketch, "E17.79.0", {"start": v(-33.23, 14.35) * mm, "end": v(-35.57, 15.34) * mm});
            skLineSegment(sketch, "E17.79.1", {"start": v(-35.57, 15.34) * mm, "end": v(-35.72, 15) * mm});
            skLineSegment(sketch, "E17.79.2", {"start": v(-35.72, 15) * mm, "end": v(-33.38, 14) * mm});
            skLineSegment(sketch, "E17.79.3", {"start": v(-33.38, 14) * mm, "end": v(-33.23, 14.35) * mm});
            skLineSegment(sketch, "E17.80.0", {"start": v(-32.4, 16.14) * mm, "end": v(-34.68, 17.26) * mm});
            skLineSegment(sketch, "E17.80.1", {"start": v(-34.68, 17.26) * mm, "end": v(-34.84, 16.92) * mm});
            skLineSegment(sketch, "E17.80.2", {"start": v(-34.84, 16.92) * mm, "end": v(-32.56, 15.8) * mm});
            skLineSegment(sketch, "E17.80.3", {"start": v(-32.56, 15.8) * mm, "end": v(-32.4, 16.14) * mm});
            skLineSegment(sketch, "E17.81.0", {"start": v(-31.47, 17.88) * mm, "end": v(-33.68, 19.13) * mm});
            skLineSegment(sketch, "E17.81.1", {"start": v(-33.68, 19.13) * mm, "end": v(-33.87, 18.8) * mm});
            skLineSegment(sketch, "E17.81.2", {"start": v(-33.87, 18.8) * mm, "end": v(-31.65, 17.55) * mm});
            skLineSegment(sketch, "E17.81.3", {"start": v(-31.65, 17.55) * mm, "end": v(-31.47, 17.88) * mm});
            skLineSegment(sketch, "E17.82.0", {"start": v(-30.44, 19.57) * mm, "end": v(-32.59, 20.94) * mm});
            skLineSegment(sketch, "E17.82.1", {"start": v(-32.59, 20.94) * mm, "end": v(-32.8, 20.61) * mm});
            skLineSegment(sketch, "E17.82.2", {"start": v(-32.8, 20.61) * mm, "end": v(-30.65, 19.25) * mm});
            skLineSegment(sketch, "E17.82.3", {"start": v(-30.65, 19.25) * mm, "end": v(-30.44, 19.57) * mm});
            skLineSegment(sketch, "E17.83.0", {"start": v(-29.33, 21.2) * mm, "end": v(-31.4, 22.68) * mm});
            skLineSegment(sketch, "E17.83.1", {"start": v(-31.4, 22.68) * mm, "end": v(-31.62, 22.37) * mm});
            skLineSegment(sketch, "E17.83.2", {"start": v(-31.62, 22.37) * mm, "end": v(-29.55, 20.9) * mm});
            skLineSegment(sketch, "E17.83.3", {"start": v(-29.55, 20.9) * mm, "end": v(-29.33, 21.2) * mm});
            skLineSegment(sketch, "E17.84.0", {"start": v(-28.13, 22.77) * mm, "end": v(-30.11, 24.36) * mm});
            skLineSegment(sketch, "E17.84.1", {"start": v(-30.11, 24.36) * mm, "end": v(-30.35, 24.06) * mm});
            skLineSegment(sketch, "E17.84.2", {"start": v(-30.35, 24.06) * mm, "end": v(-28.37, 22.48) * mm});
            skLineSegment(sketch, "E17.84.3", {"start": v(-28.37, 22.48) * mm, "end": v(-28.13, 22.77) * mm});
            skLineSegment(sketch, "E17.85.0", {"start": v(-26.85, 24.27) * mm, "end": v(-28.74, 25.97) * mm});
            skLineSegment(sketch, "E17.85.1", {"start": v(-28.74, 25.97) * mm, "end": v(-29, 25.69) * mm});
            skLineSegment(sketch, "E17.85.2", {"start": v(-29, 25.69) * mm, "end": v(-27.1, 24) * mm});
            skLineSegment(sketch, "E17.85.3", {"start": v(-27.1, 24) * mm, "end": v(-26.85, 24.27) * mm});
            skLineSegment(sketch, "E17.86.0", {"start": v(-25.48, 25.7) * mm, "end": v(-27.28, 27.5) * mm});
            skLineSegment(sketch, "E17.86.1", {"start": v(-27.28, 27.5) * mm, "end": v(-27.55, 27.23) * mm});
            skLineSegment(sketch, "E17.86.2", {"start": v(-27.55, 27.23) * mm, "end": v(-25.75, 25.43) * mm});
            skLineSegment(sketch, "E17.86.3", {"start": v(-25.75, 25.43) * mm, "end": v(-25.48, 25.7) * mm});
            skLineSegment(sketch, "E17.87.0", {"start": v(-24.04, 27.06) * mm, "end": v(-25.74, 28.95) * mm});
            skLineSegment(sketch, "E17.87.1", {"start": v(-25.74, 28.95) * mm, "end": v(-26.02, 28.7) * mm});
            skLineSegment(sketch, "E17.87.2", {"start": v(-26.02, 28.7) * mm, "end": v(-24.33, 26.8) * mm});
            skLineSegment(sketch, "E17.87.3", {"start": v(-24.33, 26.8) * mm, "end": v(-24.04, 27.06) * mm});
            skLineSegment(sketch, "E17.88.0", {"start": v(-22.53, 28.33) * mm, "end": v(-24.12, 30.3) * mm});
            skLineSegment(sketch, "E17.88.1", {"start": v(-24.12, 30.3) * mm, "end": v(-24.42, 30.07) * mm});
            skLineSegment(sketch, "E17.88.2", {"start": v(-24.42, 30.07) * mm, "end": v(-22.83, 28.09) * mm});
            skLineSegment(sketch, "E17.88.3", {"start": v(-22.83, 28.09) * mm, "end": v(-22.53, 28.33) * mm});
            skLineSegment(sketch, "E17.89.0", {"start": v(-20.95, 29.51) * mm, "end": v(-22.43, 31.58) * mm});
            skLineSegment(sketch, "E17.89.1", {"start": v(-22.43, 31.58) * mm, "end": v(-22.74, 31.36) * mm});
            skLineSegment(sketch, "E17.89.2", {"start": v(-22.74, 31.36) * mm, "end": v(-21.26, 29.3) * mm});
            skLineSegment(sketch, "E17.89.3", {"start": v(-21.26, 29.3) * mm, "end": v(-20.95, 29.51) * mm});
            skLineSegment(sketch, "E17.90.0", {"start": v(-19.31, 30.61) * mm, "end": v(-20.68, 32.75) * mm});
            skLineSegment(sketch, "E17.90.1", {"start": v(-20.68, 32.75) * mm, "end": v(-21, 32.55) * mm});
            skLineSegment(sketch, "E17.90.2", {"start": v(-21, 32.55) * mm, "end": v(-19.63, 30.4) * mm});
            skLineSegment(sketch, "E17.90.3", {"start": v(-19.63, 30.4) * mm, "end": v(-19.31, 30.61) * mm});
            skLineSegment(sketch, "E17.91.0", {"start": v(-17.61, 31.62) * mm, "end": v(-18.86, 33.83) * mm});
            skLineSegment(sketch, "E17.91.1", {"start": v(-18.86, 33.83) * mm, "end": v(-19.2, 33.65) * mm});
            skLineSegment(sketch, "E17.91.2", {"start": v(-19.2, 33.65) * mm, "end": v(-17.94, 31.43) * mm});
            skLineSegment(sketch, "E17.91.3", {"start": v(-17.94, 31.43) * mm, "end": v(-17.61, 31.62) * mm});
            skLineSegment(sketch, "E17.92.0", {"start": v(-15.86, 32.53) * mm, "end": v(-16.99, 34.81) * mm});
            skLineSegment(sketch, "E17.92.1", {"start": v(-16.99, 34.81) * mm, "end": v(-17.33, 34.64) * mm});
            skLineSegment(sketch, "E17.92.2", {"start": v(-17.33, 34.64) * mm, "end": v(-16.2, 32.37) * mm});
            skLineSegment(sketch, "E17.92.3", {"start": v(-16.2, 32.37) * mm, "end": v(-15.86, 32.53) * mm});
            skLineSegment(sketch, "E17.93.0", {"start": v(-14.06, 33.35) * mm, "end": v(-15.06, 35.69) * mm});
            skLineSegment(sketch, "E17.93.1", {"start": v(-15.06, 35.69) * mm, "end": v(-15.41, 35.54) * mm});
            skLineSegment(sketch, "E17.93.2", {"start": v(-15.41, 35.54) * mm, "end": v(-14.41, 33.2) * mm});
            skLineSegment(sketch, "E17.93.3", {"start": v(-14.41, 33.2) * mm, "end": v(-14.06, 33.35) * mm});
            skLineSegment(sketch, "E17.94.0", {"start": v(-12.22, 34.07) * mm, "end": v(-13.1, 36.46) * mm});
            skLineSegment(sketch, "E17.94.1", {"start": v(-13.1, 36.46) * mm, "end": v(-13.45, 36.32) * mm});
            skLineSegment(sketch, "E17.94.2", {"start": v(-13.45, 36.32) * mm, "end": v(-12.58, 33.94) * mm});
            skLineSegment(sketch, "E17.94.3", {"start": v(-12.58, 33.94) * mm, "end": v(-12.22, 34.07) * mm});
            skLineSegment(sketch, "E17.95.0", {"start": v(-10.34, 34.68) * mm, "end": v(-11.08, 37.12) * mm});
            skLineSegment(sketch, "E17.95.1", {"start": v(-11.08, 37.12) * mm, "end": v(-11.45, 37) * mm});
            skLineSegment(sketch, "E17.95.2", {"start": v(-11.45, 37) * mm, "end": v(-10.7, 34.57) * mm});
            skLineSegment(sketch, "E17.95.3", {"start": v(-10.7, 34.57) * mm, "end": v(-10.34, 34.68) * mm});
            skLineSegment(sketch, "E17.96.0", {"start": v(-8.44, 35.2) * mm, "end": v(-9.04, 37.66) * mm});
            skLineSegment(sketch, "E17.96.1", {"start": v(-9.04, 37.66) * mm, "end": v(-9.41, 37.57) * mm});
            skLineSegment(sketch, "E17.96.2", {"start": v(-9.41, 37.57) * mm, "end": v(-8.8, 35.1) * mm});
            skLineSegment(sketch, "E17.96.3", {"start": v(-8.8, 35.1) * mm, "end": v(-8.44, 35.2) * mm});
            skLineSegment(sketch, "E17.97.0", {"start": v(-6.5, 35.6) * mm, "end": v(-6.97, 38.1) * mm});
            skLineSegment(sketch, "E17.97.1", {"start": v(-6.97, 38.1) * mm, "end": v(-7.35, 38.03) * mm});
            skLineSegment(sketch, "E17.97.2", {"start": v(-7.35, 38.03) * mm, "end": v(-6.88, 35.53) * mm});
            skLineSegment(sketch, "E17.97.3", {"start": v(-6.88, 35.53) * mm, "end": v(-6.5, 35.6) * mm});
            skLineSegment(sketch, "E17.98.0", {"start": v(-4.55, 35.9) * mm, "end": v(-4.89, 38.43) * mm});
            skLineSegment(sketch, "E17.98.1", {"start": v(-4.89, 38.43) * mm, "end": v(-5.26, 38.38) * mm});
            skLineSegment(sketch, "E17.98.2", {"start": v(-5.26, 38.38) * mm, "end": v(-4.93, 35.86) * mm});
            skLineSegment(sketch, "E17.98.3", {"start": v(-4.93, 35.86) * mm, "end": v(-4.55, 35.9) * mm});
            skLineSegment(sketch, "E17.99.0", {"start": v(-2.59, 36.1) * mm, "end": v(-2.78, 38.63) * mm});
            skLineSegment(sketch, "E17.99.1", {"start": v(-2.78, 38.63) * mm, "end": v(-3.16, 38.6) * mm});
            skLineSegment(sketch, "E17.99.2", {"start": v(-3.16, 38.6) * mm, "end": v(-2.97, 36.07) * mm});
            skLineSegment(sketch, "E17.99.3", {"start": v(-2.97, 36.07) * mm, "end": v(-2.59, 36.1) * mm});
            skLineSegment(sketch, "E17.100.0", {"start": v(-0.61, 36.19) * mm, "end": v(-0.67, 38.73) * mm});
            skLineSegment(sketch, "E17.100.1", {"start": v(-0.67, 38.73) * mm, "end": v(-1.05, 38.72) * mm});
            skLineSegment(sketch, "E17.100.2", {"start": v(-1.05, 38.72) * mm, "end": v(-1, 36.18) * mm});
            skLineSegment(sketch, "E17.100.3", {"start": v(-1, 36.18) * mm, "end": v(-0.61, 36.19) * mm});
            skLineSegment(sketch, "E17.101.0", {"start": v(1.36, 36.17) * mm, "end": v(1.44, 38.7) * mm});
            skLineSegment(sketch, "E17.101.1", {"start": v(1.44, 38.7) * mm, "end": v(1.06, 38.72) * mm});
            skLineSegment(sketch, "E17.101.2", {"start": v(1.06, 38.72) * mm, "end": v(0.98, 36.18) * mm});
            skLineSegment(sketch, "E17.101.3", {"start": v(0.98, 36.18) * mm, "end": v(1.36, 36.17) * mm});
            skLineSegment(sketch, "E17.102.0", {"start": v(3.33, 36.04) * mm, "end": v(3.55, 38.57) * mm});
            skLineSegment(sketch, "E17.102.1", {"start": v(3.55, 38.57) * mm, "end": v(3.17, 38.6) * mm});
            skLineSegment(sketch, "E17.102.2", {"start": v(3.17, 38.6) * mm, "end": v(2.95, 36.07) * mm});
            skLineSegment(sketch, "E17.102.3", {"start": v(2.95, 36.07) * mm, "end": v(3.33, 36.04) * mm});
            skLineSegment(sketch, "E17.103.0", {"start": v(5.3, 35.8) * mm, "end": v(5.65, 38.32) * mm});
            skLineSegment(sketch, "E17.103.1", {"start": v(5.65, 38.32) * mm, "end": v(5.28, 38.37) * mm});
            skLineSegment(sketch, "E17.103.2", {"start": v(5.28, 38.37) * mm, "end": v(4.92, 35.86) * mm});
            skLineSegment(sketch, "E17.103.3", {"start": v(4.92, 35.86) * mm, "end": v(5.3, 35.8) * mm});
            skLineSegment(sketch, "E17.104.0", {"start": v(7.24, 35.46) * mm, "end": v(7.73, 37.95) * mm});
            skLineSegment(sketch, "E17.104.1", {"start": v(7.73, 37.95) * mm, "end": v(7.36, 38.03) * mm});
            skLineSegment(sketch, "E17.104.2", {"start": v(7.36, 38.03) * mm, "end": v(6.87, 35.54) * mm});
            skLineSegment(sketch, "E17.104.3", {"start": v(6.87, 35.54) * mm, "end": v(7.24, 35.46) * mm});
            skLineSegment(sketch, "E17.105.0", {"start": v(9.16, 35.02) * mm, "end": v(9.8, 37.48) * mm});
            skLineSegment(sketch, "E17.105.1", {"start": v(9.8, 37.48) * mm, "end": v(9.42, 37.57) * mm});
            skLineSegment(sketch, "E17.105.2", {"start": v(9.42, 37.57) * mm, "end": v(8.8, 35.1) * mm});
            skLineSegment(sketch, "E17.105.3", {"start": v(8.8, 35.1) * mm, "end": v(9.16, 35.02) * mm});
            skLineSegment(sketch, "E17.106.0", {"start": v(11.06, 34.46) * mm, "end": v(11.82, 36.89) * mm});
            skLineSegment(sketch, "E17.106.1", {"start": v(11.82, 36.89) * mm, "end": v(11.46, 37) * mm});
            skLineSegment(sketch, "E17.106.2", {"start": v(11.46, 37) * mm, "end": v(10.7, 34.58) * mm});
            skLineSegment(sketch, "E17.106.3", {"start": v(10.7, 34.58) * mm, "end": v(11.06, 34.46) * mm});
            skLineSegment(sketch, "E17.107.0", {"start": v(12.92, 33.8) * mm, "end": v(13.82, 36.19) * mm});
            skLineSegment(sketch, "E17.107.1", {"start": v(13.82, 36.19) * mm, "end": v(13.46, 36.32) * mm});
            skLineSegment(sketch, "E17.107.2", {"start": v(13.46, 36.32) * mm, "end": v(12.57, 33.94) * mm});
            skLineSegment(sketch, "E17.107.3", {"start": v(12.57, 33.94) * mm, "end": v(12.92, 33.8) * mm});
            skLineSegment(sketch, "E17.108.0", {"start": v(14.75, 33.05) * mm, "end": v(15.77, 35.38) * mm});
            skLineSegment(sketch, "E17.108.1", {"start": v(15.77, 35.38) * mm, "end": v(15.42, 35.53) * mm});
            skLineSegment(sketch, "E17.108.2", {"start": v(15.42, 35.53) * mm, "end": v(14.4, 33.2) * mm});
            skLineSegment(sketch, "E17.108.3", {"start": v(14.4, 33.2) * mm, "end": v(14.75, 33.05) * mm});
            skLineSegment(sketch, "E17.109.0", {"start": v(16.53, 32.2) * mm, "end": v(17.68, 34.47) * mm});
            skLineSegment(sketch, "E17.109.1", {"start": v(17.68, 34.47) * mm, "end": v(17.34, 34.64) * mm});
            skLineSegment(sketch, "E17.109.2", {"start": v(17.34, 34.64) * mm, "end": v(16.2, 32.37) * mm});
            skLineSegment(sketch, "E17.109.3", {"start": v(16.2, 32.37) * mm, "end": v(16.53, 32.2) * mm});
            skPoint(sketch, "E17.center", {"position": v(0, 0) * mm});
            skLineSegment(sketch, "E17.anchor1", {"start": v(0, 0) * mm, "end": v(26.17, 25) * mm, "construction": true});
            skLineSegment(sketch, "E17.anchor2", {"start": v(0, 0) * mm, "end": v(18.26, 31.25) * mm, "construction": true});
            skLineSegment(sketch, "E18.1.110.0", {"start": v(18.26, 31.25) * mm, "end": v(19.53, 33.45) * mm});
            skLineSegment(sketch, "E18.3.110.0", {"start": v(19.53, 33.45) * mm, "end": v(19.2, 33.64) * mm});
            skLineSegment(sketch, "E18.6.110.0", {"start": v(19.2, 33.64) * mm, "end": v(17.93, 31.44) * mm});
            skLineSegment(sketch, "E18.9.110.0", {"start": v(17.93, 31.44) * mm, "end": v(18.26, 31.25) * mm});
            skSolve(sketch);
        }
        {
            var Q0;
            Q0 = qSketchRegion(id + "F4", true);
            extrude(context, id + "F5", {"entities" : qUnion([Q0]), "depth" : 0.03 * mm});
        }
        {
            var Q0;
            {var subQ271=sQuery(id+"F4.wireOp",EDGE,"E14");Q0=makeQuery(id+"F4.imprint","IMPRINT",FACE,{"disambiguationData":[TD([[makeQuery(id+"F4.imprint","IMPRINT",EDGE,{"derivedFrom":subQ271}),-1.0]])]});}
            var sketch = newSketch(context, id + "F6", { "sketchPlane" : qUnion([Q0])});
            skLineSegment(sketch, "E19.0", {"start": v(24.34, 23.24) * mm, "end": v(28, 26.77) * mm});
            skLineSegment(sketch, "E19.1", {"start": v(24.08, 23.51) * mm, "end": v(24.34, 23.24) * mm});
            skLineSegment(sketch, "E19.2", {"start": v(27.73, 27.04) * mm, "end": v(24.08, 23.51) * mm});
            skLineSegment(sketch, "E19.3", {"start": v(28, 26.77) * mm, "end": v(27.73, 27.04) * mm});
            skLineSegment(sketch, "E20.1.0", {"start": v(29.7, 15.82) * mm, "end": v(34.17, 18.23) * mm});
            skLineSegment(sketch, "E20.1.1", {"start": v(34, 18.57) * mm, "end": v(29.52, 16.16) * mm});
            skLineSegment(sketch, "E20.1.2", {"start": v(34.17, 18.23) * mm, "end": v(34, 18.57) * mm});
            skLineSegment(sketch, "E20.1.3", {"start": v(29.52, 16.16) * mm, "end": v(29.7, 15.82) * mm});
            skLineSegment(sketch, "E20.2.0", {"start": v(32.87, 7.23) * mm, "end": v(37.82, 8.35) * mm});
            skLineSegment(sketch, "E20.2.1", {"start": v(37.74, 8.72) * mm, "end": v(32.78, 7.6) * mm});
            skLineSegment(sketch, "E20.2.2", {"start": v(37.82, 8.35) * mm, "end": v(37.74, 8.72) * mm});
            skLineSegment(sketch, "E20.2.3", {"start": v(32.78, 7.6) * mm, "end": v(32.87, 7.23) * mm});
            skLineSegment(sketch, "E20.3.0", {"start": v(33.6, -1.9) * mm, "end": v(38.67, -2.16) * mm});
            skLineSegment(sketch, "E20.3.1", {"start": v(38.7, -1.78) * mm, "end": v(33.62, -1.52) * mm});
            skLineSegment(sketch, "E20.3.2", {"start": v(38.67, -2.16) * mm, "end": v(38.7, -1.78) * mm});
            skLineSegment(sketch, "E20.3.3", {"start": v(33.62, -1.52) * mm, "end": v(33.6, -1.9) * mm});
            skLineSegment(sketch, "E20.4.0", {"start": v(31.84, -10.88) * mm, "end": v(36.66, -12.5) * mm});
            skLineSegment(sketch, "E20.4.1", {"start": v(36.78, -12.14) * mm, "end": v(31.97, -10.52) * mm});
            skLineSegment(sketch, "E20.4.2", {"start": v(36.66, -12.5) * mm, "end": v(36.78, -12.14) * mm});
            skLineSegment(sketch, "E20.4.3", {"start": v(31.97, -10.52) * mm, "end": v(31.84, -10.88) * mm});
            skLineSegment(sketch, "E20.5.0", {"start": v(27.73, -19.06) * mm, "end": v(31.94, -21.92) * mm});
            skLineSegment(sketch, "E20.5.1", {"start": v(32.15, -21.6) * mm, "end": v(27.95, -18.75) * mm});
            skLineSegment(sketch, "E20.5.2", {"start": v(31.94, -21.92) * mm, "end": v(32.15, -21.6) * mm});
            skLineSegment(sketch, "E20.5.3", {"start": v(27.95, -18.75) * mm, "end": v(27.73, -19.06) * mm});
            skLineSegment(sketch, "E20.6.0", {"start": v(21.57, -25.83) * mm, "end": v(24.85, -29.72) * mm});
            skLineSegment(sketch, "E20.6.1", {"start": v(25.14, -29.47) * mm, "end": v(21.86, -25.59) * mm});
            skLineSegment(sketch, "E20.6.2", {"start": v(24.85, -29.72) * mm, "end": v(25.14, -29.47) * mm});
            skLineSegment(sketch, "E20.6.3", {"start": v(21.86, -25.59) * mm, "end": v(21.57, -25.83) * mm});
            skLineSegment(sketch, "E20.7.0", {"start": v(13.8, -30.7) * mm, "end": v(15.92, -35.31) * mm});
            skLineSegment(sketch, "E20.7.1", {"start": v(16.26, -35.16) * mm, "end": v(14.15, -30.53) * mm});
            skLineSegment(sketch, "E20.7.2", {"start": v(15.92, -35.31) * mm, "end": v(16.26, -35.16) * mm});
            skLineSegment(sketch, "E20.7.3", {"start": v(14.15, -30.53) * mm, "end": v(13.8, -30.7) * mm});
            skLineSegment(sketch, "E20.8.0", {"start": v(5.02, -33.28) * mm, "end": v(5.81, -38.3) * mm});
            skLineSegment(sketch, "E20.8.1", {"start": v(6.19, -38.24) * mm, "end": v(5.4, -33.22) * mm});
            skLineSegment(sketch, "E20.8.2", {"start": v(5.81, -38.3) * mm, "end": v(6.19, -38.24) * mm});
            skLineSegment(sketch, "E20.8.3", {"start": v(5.4, -33.22) * mm, "end": v(5.02, -33.28) * mm});
            skLineSegment(sketch, "E20.9.0", {"start": v(-4.13, -33.4) * mm, "end": v(-4.73, -38.45) * mm});
            skLineSegment(sketch, "E20.9.1", {"start": v(-4.35, -38.5) * mm, "end": v(-3.75, -33.44) * mm});
            skLineSegment(sketch, "E20.9.2", {"start": v(-4.73, -38.45) * mm, "end": v(-4.35, -38.5) * mm});
            skLineSegment(sketch, "E20.9.3", {"start": v(-3.75, -33.44) * mm, "end": v(-4.13, -33.4) * mm});
            skLineSegment(sketch, "E20.10.0", {"start": v(-12.98, -31.05) * mm, "end": v(-14.91, -35.75) * mm});
            skLineSegment(sketch, "E20.10.1", {"start": v(-14.56, -35.9) * mm, "end": v(-12.63, -31.2) * mm});
            skLineSegment(sketch, "E20.10.2", {"start": v(-14.91, -35.75) * mm, "end": v(-14.56, -35.9) * mm});
            skLineSegment(sketch, "E20.10.3", {"start": v(-12.63, -31.2) * mm, "end": v(-12.98, -31.05) * mm});
            skLineSegment(sketch, "E20.11.0", {"start": v(-20.87, -26.4) * mm, "end": v(-24, -30.4) * mm});
            skLineSegment(sketch, "E20.11.1", {"start": v(-23.7, -30.64) * mm, "end": v(-20.57, -26.64) * mm});
            skLineSegment(sketch, "E20.11.2", {"start": v(-24, -30.4) * mm, "end": v(-23.7, -30.64) * mm});
            skLineSegment(sketch, "E20.11.3", {"start": v(-20.57, -26.64) * mm, "end": v(-20.87, -26.4) * mm});
            skLineSegment(sketch, "E20.12.0", {"start": v(-27.21, -19.8) * mm, "end": v(-31.3, -22.81) * mm});
            skLineSegment(sketch, "E20.12.1", {"start": v(-31.08, -23.12) * mm, "end": v(-26.99, -20.1) * mm});
            skLineSegment(sketch, "E20.12.2", {"start": v(-31.3, -22.81) * mm, "end": v(-31.08, -23.12) * mm});
            skLineSegment(sketch, "E20.12.3", {"start": v(-26.99, -20.1) * mm, "end": v(-27.21, -19.8) * mm});
            skLineSegment(sketch, "E20.13.0", {"start": v(-31.54, -11.73) * mm, "end": v(-36.3, -13.53) * mm});
            skLineSegment(sketch, "E20.13.1", {"start": v(-36.16, -13.89) * mm, "end": v(-31.4, -12.09) * mm});
            skLineSegment(sketch, "E20.13.2", {"start": v(-36.3, -13.53) * mm, "end": v(-36.16, -13.89) * mm});
            skLineSegment(sketch, "E20.13.3", {"start": v(-31.4, -12.09) * mm, "end": v(-31.54, -11.73) * mm});
            skLineSegment(sketch, "E20.14.0", {"start": v(-33.54, -2.8) * mm, "end": v(-38.6, -3.25) * mm});
            skLineSegment(sketch, "E20.14.1", {"start": v(-38.56, -3.63) * mm, "end": v(-33.5, -3.18) * mm});
            skLineSegment(sketch, "E20.14.2", {"start": v(-38.6, -3.25) * mm, "end": v(-38.56, -3.63) * mm});
            skLineSegment(sketch, "E20.14.3", {"start": v(-33.5, -3.18) * mm, "end": v(-33.54, -2.8) * mm});
            skLineSegment(sketch, "E20.15.0", {"start": v(-33.05, 6.35) * mm, "end": v(-38.05, 7.28) * mm});
            skLineSegment(sketch, "E20.15.1", {"start": v(-38.12, 6.9) * mm, "end": v(-33.12, 5.97) * mm});
            skLineSegment(sketch, "E20.15.2", {"start": v(-38.05, 7.28) * mm, "end": v(-38.12, 6.9) * mm});
            skLineSegment(sketch, "E20.15.3", {"start": v(-33.12, 5.97) * mm, "end": v(-33.05, 6.35) * mm});
            skLineSegment(sketch, "E20.16.0", {"start": v(-30.12, 15.02) * mm, "end": v(-34.68, 17.26) * mm});
            skLineSegment(sketch, "E20.16.1", {"start": v(-34.84, 16.92) * mm, "end": v(-30.28, 14.68) * mm});
            skLineSegment(sketch, "E20.16.2", {"start": v(-34.68, 17.26) * mm, "end": v(-34.84, 16.92) * mm});
            skLineSegment(sketch, "E20.16.3", {"start": v(-30.28, 14.68) * mm, "end": v(-30.12, 15.02) * mm});
            skLineSegment(sketch, "E20.17.0", {"start": v(-24.95, 22.58) * mm, "end": v(-28.74, 25.97) * mm});
            skLineSegment(sketch, "E20.17.1", {"start": v(-29, 25.69) * mm, "end": v(-25.2, 22.3) * mm});
            skLineSegment(sketch, "E20.17.2", {"start": v(-28.74, 25.97) * mm, "end": v(-29, 25.69) * mm});
            skLineSegment(sketch, "E20.17.3", {"start": v(-25.2, 22.3) * mm, "end": v(-24.95, 22.58) * mm});
            skLineSegment(sketch, "E20.18.0", {"start": v(-17.94, 28.47) * mm, "end": v(-20.68, 32.75) * mm});
            skLineSegment(sketch, "E20.18.1", {"start": v(-21, 32.55) * mm, "end": v(-18.26, 28.27) * mm});
            skLineSegment(sketch, "E20.18.2", {"start": v(-20.68, 32.75) * mm, "end": v(-21, 32.55) * mm});
            skLineSegment(sketch, "E20.18.3", {"start": v(-18.26, 28.27) * mm, "end": v(-17.94, 28.47) * mm});
            skLineSegment(sketch, "E20.19.0", {"start": v(-9.6, 32.25) * mm, "end": v(-11.08, 37.12) * mm});
            skLineSegment(sketch, "E20.19.1", {"start": v(-11.45, 37) * mm, "end": v(-9.97, 32.14) * mm});
            skLineSegment(sketch, "E20.19.2", {"start": v(-11.08, 37.12) * mm, "end": v(-11.45, 37) * mm});
            skLineSegment(sketch, "E20.19.3", {"start": v(-9.97, 32.14) * mm, "end": v(-9.6, 32.25) * mm});
            skLineSegment(sketch, "E20.20.0", {"start": v(-0.56, 33.65) * mm, "end": v(-0.67, 38.73) * mm});
            skLineSegment(sketch, "E20.20.1", {"start": v(-1.05, 38.72) * mm, "end": v(-0.94, 33.64) * mm});
            skLineSegment(sketch, "E20.20.2", {"start": v(-0.67, 38.73) * mm, "end": v(-1.05, 38.72) * mm});
            skLineSegment(sketch, "E20.20.3", {"start": v(-0.94, 33.64) * mm, "end": v(-0.56, 33.65) * mm});
            skLineSegment(sketch, "E20.21.0", {"start": v(8.53, 32.55) * mm, "end": v(9.8, 37.48) * mm});
            skLineSegment(sketch, "E20.21.1", {"start": v(9.42, 37.57) * mm, "end": v(8.16, 32.65) * mm});
            skLineSegment(sketch, "E20.21.2", {"start": v(9.8, 37.48) * mm, "end": v(9.42, 37.57) * mm});
            skLineSegment(sketch, "E20.21.3", {"start": v(8.16, 32.65) * mm, "end": v(8.53, 32.55) * mm});
            skPoint(sketch, "E20.center", {"position": v(0, 0) * mm});
            skLineSegment(sketch, "E20.anchor1", {"start": v(0, 0) * mm, "end": v(24.34, 23.24) * mm, "construction": true});
            skLineSegment(sketch, "E20.anchor2", {"start": v(0, 0) * mm, "end": v(17, 29.05) * mm, "construction": true});
            skLineSegment(sketch, "E21.1.22.0", {"start": v(17, 29.05) * mm, "end": v(19.53, 33.45) * mm});
            skLineSegment(sketch, "E21.3.22.0", {"start": v(19.2, 33.64) * mm, "end": v(16.66, 29.24) * mm});
            skLineSegment(sketch, "E21.6.22.0", {"start": v(19.53, 33.45) * mm, "end": v(19.2, 33.64) * mm});
            skLineSegment(sketch, "E21.9.22.0", {"start": v(16.66, 29.24) * mm, "end": v(17, 29.05) * mm});
            skSolve(sketch);
        }
        {
            var Q0;
            Q0 = qSketchRegion(id + "F6", true);
            extrude(context, id + "F7", {"entities" : qUnion([Q0]), "depth" : 0.05 * mm});
        }
        {
            var Q0;
            {var subQ108=sQuery(id+"F4.wireOp",EDGE,"E14");Q0=makeQuery(id+"F4.imprint","IMPRINT",FACE,{"disambiguationData":[TD([[makeQuery(id+"F4.imprint","IMPRINT",EDGE,{"derivedFrom":subQ108}),-1.0]])]});}
            var sketch = newSketch(context, id + "F8", { "sketchPlane" : qUnion([Q0])});
            skLineSegment(sketch, "E22.0", {"start": v(27.6, 27.18) * mm, "end": v(23.94, 23.65) * mm});
            skLineSegment(sketch, "E22.1", {"start": v(28.13, 26.63) * mm, "end": v(27.6, 27.18) * mm});
            skLineSegment(sketch, "E22.2", {"start": v(24.47, 23.1) * mm, "end": v(28.13, 26.63) * mm});
            skLineSegment(sketch, "E22.3", {"start": v(23.94, 23.65) * mm, "end": v(24.47, 23.1) * mm});
            skLineSegment(sketch, "E23.1.0", {"start": v(32.91, 7.04) * mm, "end": v(37.87, 8.16) * mm});
            skLineSegment(sketch, "E23.1.1", {"start": v(37.7, 8.9) * mm, "end": v(32.74, 7.79) * mm});
            skLineSegment(sketch, "E23.1.2", {"start": v(37.87, 8.16) * mm, "end": v(37.7, 8.9) * mm});
            skLineSegment(sketch, "E23.1.3", {"start": v(32.74, 7.79) * mm, "end": v(32.91, 7.04) * mm});
            skLineSegment(sketch, "E23.2.0", {"start": v(31.78, -11.06) * mm, "end": v(36.6, -12.68) * mm});
            skLineSegment(sketch, "E23.2.1", {"start": v(36.84, -11.96) * mm, "end": v(32.03, -10.34) * mm});
            skLineSegment(sketch, "E23.2.2", {"start": v(36.6, -12.68) * mm, "end": v(36.84, -11.96) * mm});
            skLineSegment(sketch, "E23.2.3", {"start": v(32.03, -10.34) * mm, "end": v(31.78, -11.06) * mm});
            skLineSegment(sketch, "E23.3.0", {"start": v(21.42, -25.96) * mm, "end": v(24.7, -29.84) * mm});
            skLineSegment(sketch, "E23.3.1", {"start": v(25.28, -29.35) * mm, "end": v(22, -25.47) * mm});
            skLineSegment(sketch, "E23.3.2", {"start": v(24.7, -29.84) * mm, "end": v(25.28, -29.35) * mm});
            skLineSegment(sketch, "E23.3.3", {"start": v(22, -25.47) * mm, "end": v(21.42, -25.96) * mm});
            skLineSegment(sketch, "E23.4.0", {"start": v(4.84, -33.3) * mm, "end": v(5.62, -38.32) * mm});
            skLineSegment(sketch, "E23.4.1", {"start": v(6.37, -38.2) * mm, "end": v(5.59, -33.19) * mm});
            skLineSegment(sketch, "E23.4.2", {"start": v(5.62, -38.32) * mm, "end": v(6.37, -38.2) * mm});
            skLineSegment(sketch, "E23.4.3", {"start": v(5.59, -33.19) * mm, "end": v(4.84, -33.3) * mm});
            skLineSegment(sketch, "E23.5.0", {"start": v(-13.16, -30.98) * mm, "end": v(-15.09, -35.67) * mm});
            skLineSegment(sketch, "E23.5.1", {"start": v(-14.38, -35.96) * mm, "end": v(-12.45, -31.27) * mm});
            skLineSegment(sketch, "E23.5.2", {"start": v(-15.09, -35.67) * mm, "end": v(-14.38, -35.96) * mm});
            skLineSegment(sketch, "E23.5.3", {"start": v(-12.45, -31.27) * mm, "end": v(-13.16, -30.98) * mm});
            skLineSegment(sketch, "E23.6.0", {"start": v(-27.33, -19.65) * mm, "end": v(-31.42, -22.66) * mm});
            skLineSegment(sketch, "E23.6.1", {"start": v(-30.96, -23.27) * mm, "end": v(-26.87, -20.26) * mm});
            skLineSegment(sketch, "E23.6.2", {"start": v(-31.42, -22.66) * mm, "end": v(-30.96, -23.27) * mm});
            skLineSegment(sketch, "E23.6.3", {"start": v(-26.87, -20.26) * mm, "end": v(-27.33, -19.65) * mm});
            skLineSegment(sketch, "E23.7.0", {"start": v(-33.55, -2.6) * mm, "end": v(-38.61, -3.06) * mm});
            skLineSegment(sketch, "E23.7.1", {"start": v(-38.55, -3.82) * mm, "end": v(-33.49, -3.37) * mm});
            skLineSegment(sketch, "E23.7.2", {"start": v(-38.61, -3.06) * mm, "end": v(-38.55, -3.82) * mm});
            skLineSegment(sketch, "E23.7.3", {"start": v(-33.49, -3.37) * mm, "end": v(-33.55, -2.6) * mm});
            skLineSegment(sketch, "E23.8.0", {"start": v(-30.03, 15.2) * mm, "end": v(-34.6, 17.43) * mm});
            skLineSegment(sketch, "E23.8.1", {"start": v(-34.93, 16.75) * mm, "end": v(-30.37, 14.5) * mm});
            skLineSegment(sketch, "E23.8.2", {"start": v(-34.6, 17.43) * mm, "end": v(-34.93, 16.75) * mm});
            skLineSegment(sketch, "E23.8.3", {"start": v(-30.37, 14.5) * mm, "end": v(-30.03, 15.2) * mm});
            skLineSegment(sketch, "E23.9.0", {"start": v(-17.78, 28.57) * mm, "end": v(-20.52, 32.86) * mm});
            skLineSegment(sketch, "E23.9.1", {"start": v(-21.16, 32.45) * mm, "end": v(-18.43, 28.16) * mm});
            skLineSegment(sketch, "E23.9.2", {"start": v(-20.52, 32.86) * mm, "end": v(-21.16, 32.45) * mm});
            skLineSegment(sketch, "E23.9.3", {"start": v(-18.43, 28.16) * mm, "end": v(-17.78, 28.57) * mm});
            skLineSegment(sketch, "E23.10.0", {"start": v(-0.37, 33.65) * mm, "end": v(-0.48, 38.73) * mm});
            skLineSegment(sketch, "E23.10.1", {"start": v(-1.24, 38.72) * mm, "end": v(-1.13, 33.64) * mm});
            skLineSegment(sketch, "E23.10.2", {"start": v(-0.48, 38.73) * mm, "end": v(-1.24, 38.72) * mm});
            skLineSegment(sketch, "E23.10.3", {"start": v(-1.13, 33.64) * mm, "end": v(-0.37, 33.65) * mm});
            skLineSegment(sketch, "E23.11.0", {"start": v(17.16, 28.95) * mm, "end": v(19.7, 33.35) * mm});
            skLineSegment(sketch, "E23.11.1", {"start": v(19.04, 33.73) * mm, "end": v(16.5, 29.33) * mm});
            skLineSegment(sketch, "E23.11.2", {"start": v(19.7, 33.35) * mm, "end": v(19.04, 33.73) * mm});
            skLineSegment(sketch, "E23.11.3", {"start": v(16.5, 29.33) * mm, "end": v(17.16, 28.95) * mm});
            skPoint(sketch, "E23.center", {"position": v(0, 0) * mm});
            skLineSegment(sketch, "E23.anchor1", {"start": v(0, 0) * mm, "end": v(24.47, 23.1) * mm, "construction": true});
            skLineSegment(sketch, "E23.anchor2", {"start": v(0, 0) * mm, "end": v(17.16, 28.95) * mm, "construction": true});
            skSolve(sketch);
        }
        {
            var Q0;
            Q0 = qSketchRegion(id + "F8", true);
            extrude(context, id + "F9", {"entities" : qUnion([Q0]), "depth" : 0.13 * mm});
        }
        {
            var Q0;
            Q0=makeQuery(id+"F1.opExtrude","CAP_FACE",FACE,{"disambiguationData":[OSD([sQuery(id+"F0.wireOp",EDGE,"E0")])],"isStart":false});
            var sketch = newSketch(context, id + "F10", { "sketchPlane" : qUnion([Q0])});
            skText(sketch, "E24", { "text": "100%", "fontName": "OpenSans-Regular.ttf"});
            skText(sketch, "E25", { "text": "ОБОРОТЫ", "fontName": "OpenSans-Bold.ttf"});
            skText(sketch, "E26", { "text": "80", "fontName": "OpenSans-Regular.ttf"});
            skText(sketch, "E27", { "text": "60", "fontName": "OpenSans-Regular.ttf"});
            skText(sketch, "E28", { "text": "40", "fontName": "OpenSans-Regular.ttf"});
            skText(sketch, "E29", { "text": "20", "fontName": "OpenSans-Regular.ttf"});
            skText(sketch, "E30", { "text": "0", "fontName": "OpenSans-Regular.ttf"});
            const initialGuessF10  = {"E24": [-0.01228, 0.02514, 1, 0, 0.00711], "E25": [-0.01202, 0.00837, 1, 0, 0.00343], "E26": [-0.03037, 0.0074, 1, 0, 0.00711], "E27": [-0.02687, -0.02316, 1, 0, 0.00711], "E28": [0.00019, -0.0307, 1, 0, 0.00711], "E29": [0.02071, -0.01106, 1, 0, 0.00729], "E30": [0.01716, 0.01874, 1, 0, 0.00711]};
            skSetInitialGuess(sketch, initialGuessF10);
            skSolve(sketch);
        }
        {
            var Q0;
            Q0 = qSketchRegion(id + "F10", true);
            extrude(context, id + "F11", {"entities" : qUnion([Q0]), "depth" : 0.03 * mm});
        }
    });
